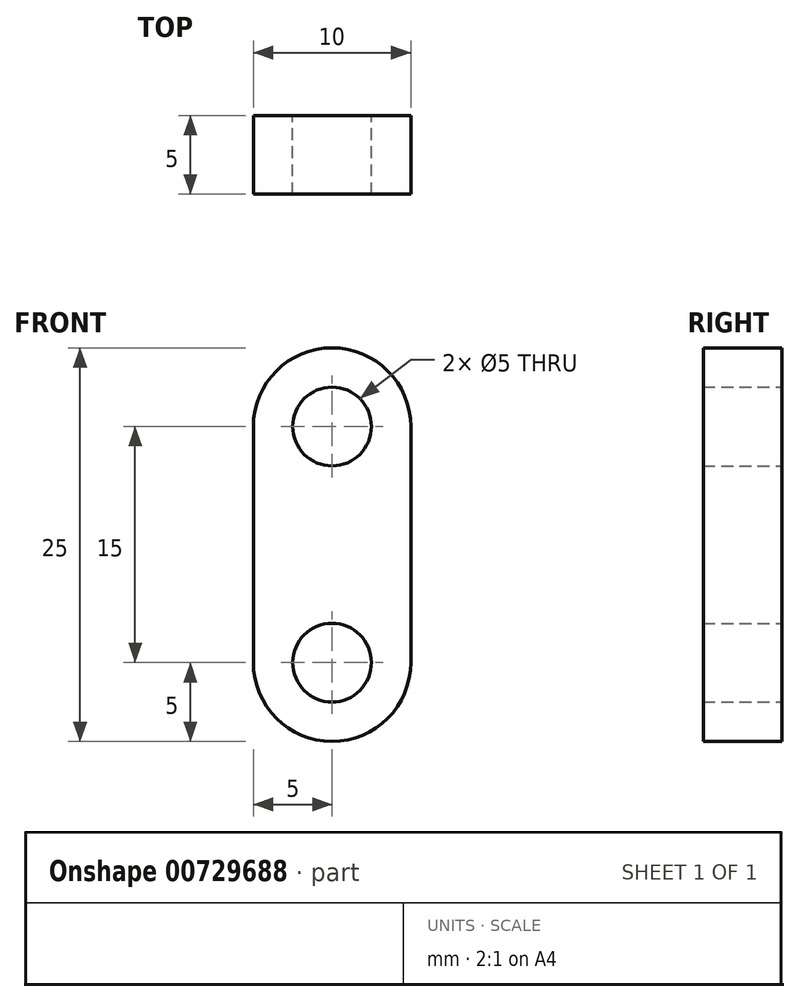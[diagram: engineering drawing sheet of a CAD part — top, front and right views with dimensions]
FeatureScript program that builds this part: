
annotation { "Feature Type Name" : "Feature", "Feature Type Description" : "" }
export const myFeature = defineFeature(function(context is Context, id is Id, definition is map)
    precondition{}
    {
        {
            var Q0;
            Q0=qCreatedBy(makeId("Front.planeOp"),FACE);
            var sketch = newSketch(context, id + "F0", { "sketchPlane" : qUnion([Q0])});
            skArc(sketch, "E0", {"start": v(5, 0) * mm, "mid": v(0, 5) * mm, "end": v(-5, 0) * mm});
            skArc(sketch, "E1", {"start": v(-5, -15) * mm, "mid": v(0, -20) * mm, "end": v(5, -15) * mm});
            skLineSegment(sketch, "E2", {"start": v(-5, 0) * mm, "end": v(-5, -15) * mm});
            skLineSegment(sketch, "E3", {"start": v(5, 0) * mm, "end": v(5, -15) * mm});
            skCircle(sketch, "E4", {"center": v(0, 0) * mm, "radius": 2.5 * mm});
            skCircle(sketch, "E5", {"center": v(0, -15) * mm, "radius": 2.5 * mm});
            skSolve(sketch);
        }
        {
            var Q0;
            Q0=makeQuery(id+"F0.imprint","IMPRINT",FACE,{"disambiguationData":[TD([[makeQuery(id+"F0.imprint","IMPRINT",EDGE,{"derivedFrom":sQuery(id+"F0.wireOp",EDGE,"E0")}),1.0]])]});
            extrude(context, id + "F1", {"entities" : qUnion([Q0]), "endBound" : BoundingType.SYMMETRIC, "depth" : 5 * mm, "offsetDistance" : 25 * mm});
        }
    });
